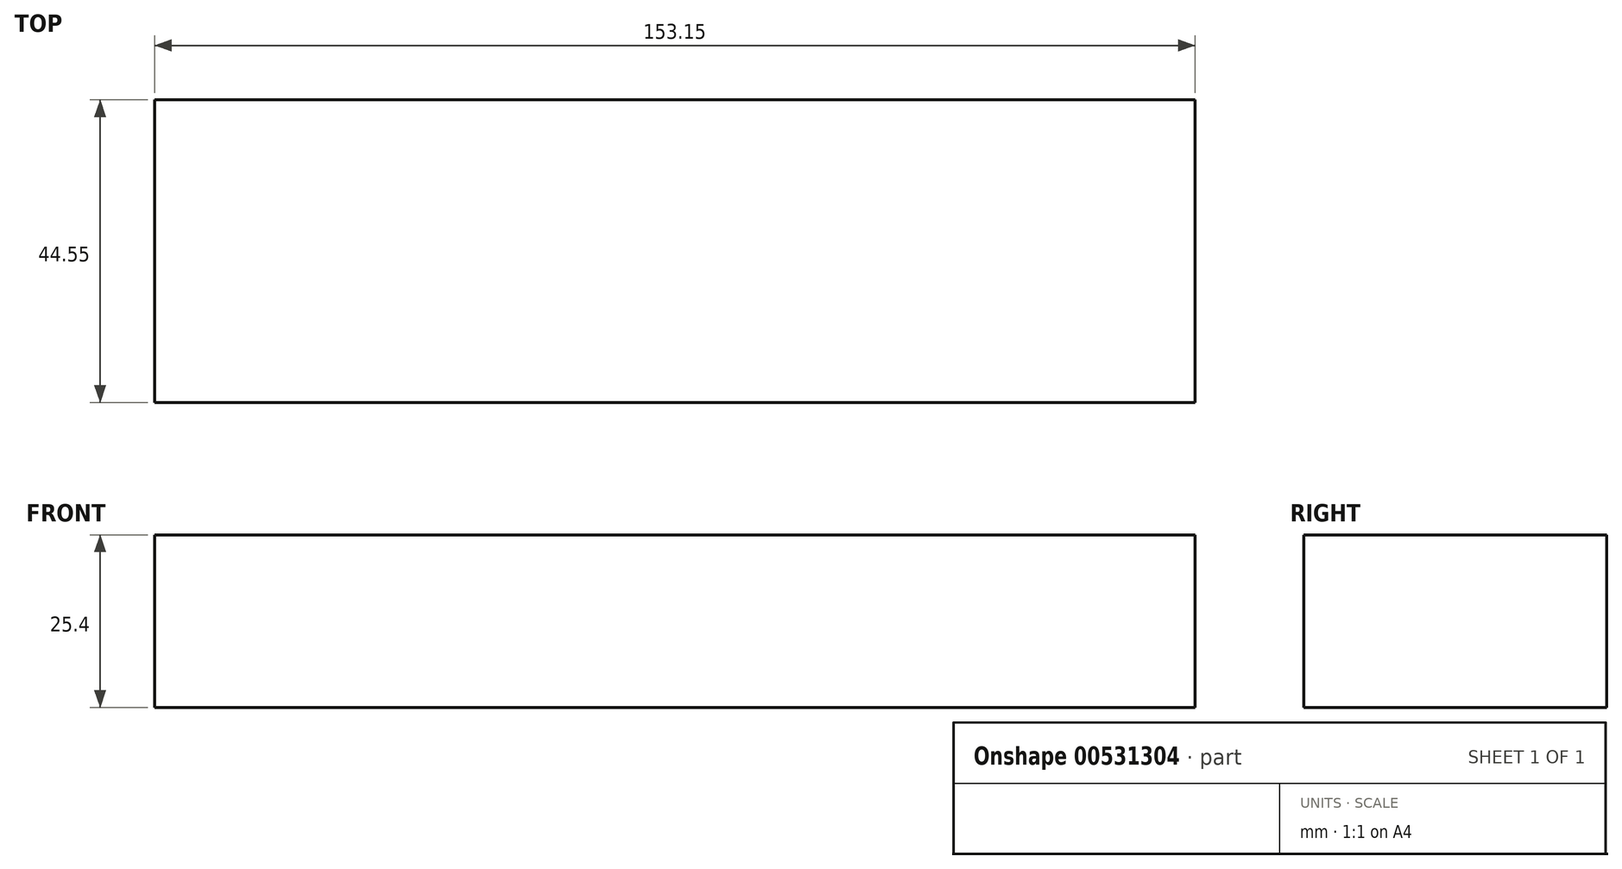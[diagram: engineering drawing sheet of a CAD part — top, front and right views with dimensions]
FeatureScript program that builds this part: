
annotation { "Feature Type Name" : "Feature", "Feature Type Description" : "" }
export const myFeature = defineFeature(function(context is Context, id is Id, definition is map)
    precondition{}
    {
        {
            var Q0;
            Q0=qCreatedBy(makeId("Top.planeOp"), FACE);
            var sketch = newSketch(context, id + "F0", { "sketchPlane" : qUnion([Q0])});
            skLineSegment(sketch, "E0", {"start": v(0, 0) * mm, "end": v(-76.7, 0) * mm});
            skLineSegment(sketch, "E1", {"start": v(-76.7, 0) * mm, "end": v(-76.7, 44.55) * mm});
            skLineSegment(sketch, "E2", {"start": v(-76.7, 44.55) * mm, "end": v(76.45, 44.55) * mm});
            skLineSegment(sketch, "E3", {"start": v(76.45, 44.55) * mm, "end": v(76.45, 0) * mm});
            skLineSegment(sketch, "E4", {"start": v(76.45, 0) * mm, "end": v(0, 0) * mm});
            skSolve(sketch);
        }
        {
            var Q0;
            Q0 = qSketchRegion(id + "F0", true);
            extrude(context, id + "F1", {"entities" : qUnion([Q0]), "depth" : 25.4 * mm, "offsetDistance" : 25.4 * mm});
        }
    });
